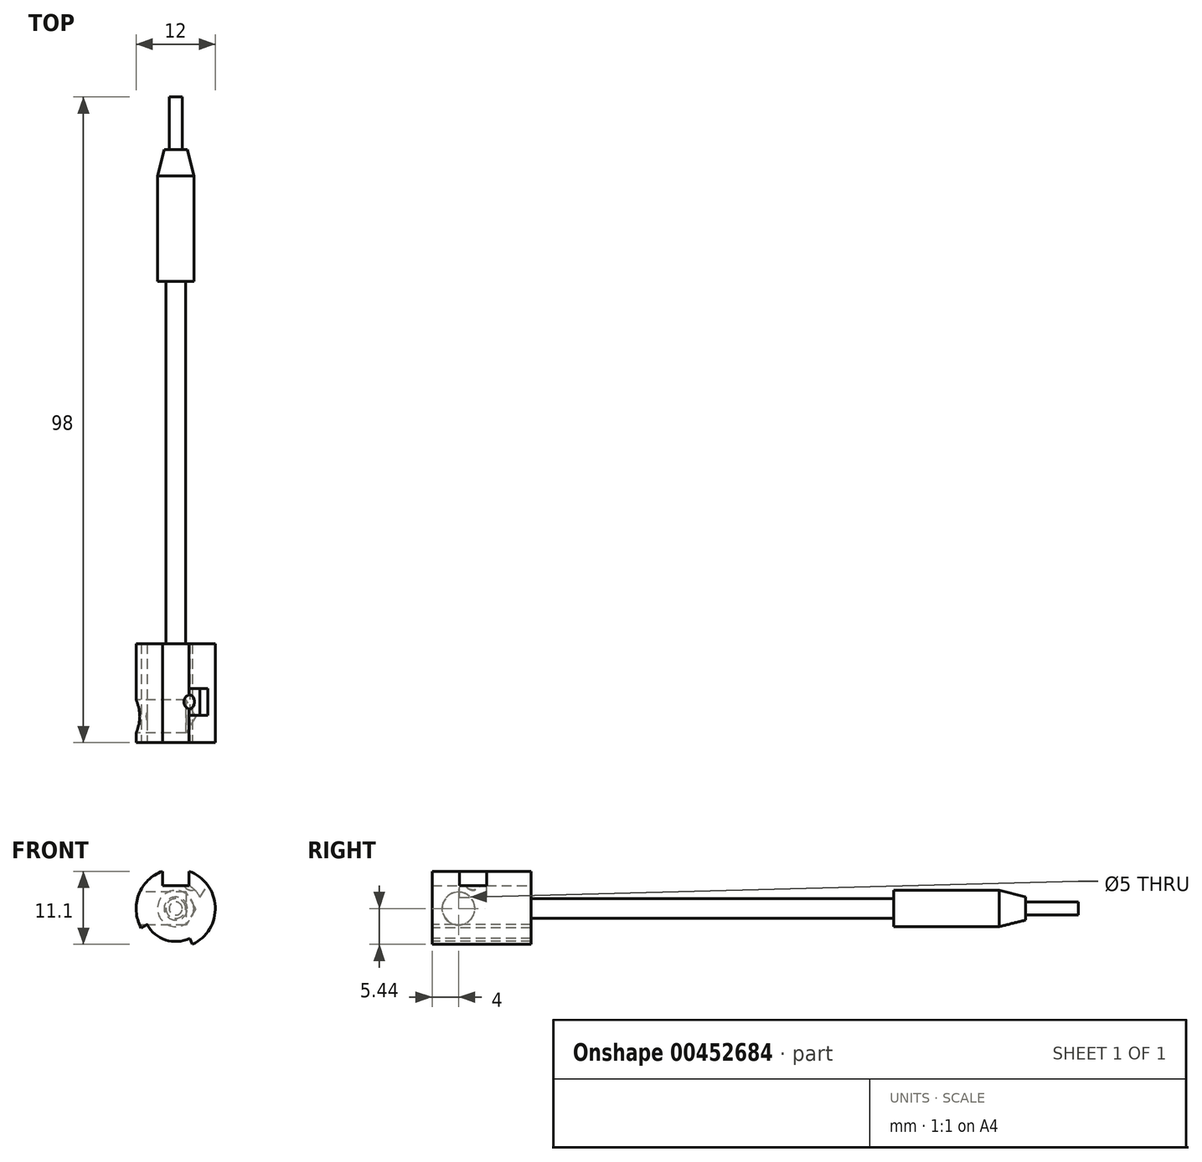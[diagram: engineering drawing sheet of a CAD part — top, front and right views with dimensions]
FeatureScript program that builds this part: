
annotation { "Feature Type Name" : "Feature", "Feature Type Description" : "" }
export const myFeature = defineFeature(function(context is Context, id is Id, definition is map)
    precondition{}
    {
        {
            var Q0;
            Q0=qCreatedBy(makeId("Front.planeOp"),FACE);
            var sketch = newSketch(context, id + "F0", { "sketchPlane" : qUnion([Q0])});
            skCircle(sketch, "E0", {"center": v(0, 0) * mm, "radius": 1 * mm});
            skSolve(sketch);
        }
        {
            var Q0;
            Q0=qSketchRegion(id+"F0",true);
            extrude(context, id + "F1", {"entities" : qUnion([Q0]), "oppositeDirection" : true, "depth" : 8 * mm});
        }
        {
            var Q0;
            Q0=makeQuery(id+"F1.opExtrude","CAP_FACE",FACE,{"disambiguationData":[OSD([sQuery(id+"F0.wireOp",EDGE,"E0")])],"isStart":true});
            var sketch = newSketch(context, id + "F2", { "sketchPlane" : qUnion([Q0])});
            skCircle(sketch, "E1", {"center": v(0, 0) * mm, "radius": 2.75 * mm});
            skSolve(sketch);
        }
        {
            var Q0;
            Q0=qSketchRegion(id+"F2",true);
            extrude(context, id + "F3", {"entities" : qUnion([Q0]), "operationType" : NewBodyOperationType.ADD, "depth" : 80 * mm});
        }
        {
            var Q0;
            Q0=makeQuery(id+"F3.opExtrude","CAP_EDGE",EDGE,{"disambiguationData":[OSD([sQuery(id+"F2.wireOp",EDGE,"E1")])],"isStart":true});
            chamfer(context, id + "F4", {"entities" : qUnion([Q0]), "chamferType" : ChamferType.TWO_OFFSETS, "width1" : 4 * mm, "oppositeDirection" : false, "width2" : 1 * mm, "tangentPropagation" : true});
        }
        {
            var Q0;
            Q0=makeQuery(id+"F3.opExtrude","CAP_FACE",FACE,{"disambiguationData":[OSD([sQuery(id+"F2.wireOp",EDGE,"E1")])],"isStart":false});
            var sketch = newSketch(context, id + "F5", { "sketchPlane" : qUnion([Q0])});
            skCircle(sketch, "E2", {"center": v(0, 0) * mm, "radius": 6 * mm});
            skSolve(sketch);
        }
        {
            var Q0;
            Q0=makeQuery(id+"F5.imprint","IMPRINT",FACE,{"disambiguationData":[TD([[makeQuery(id+"F5.imprint","IMPRINT",EDGE,{"derivedFrom":sQuery(id+"F5.wireOp",EDGE,"E2")}),1.0]])]});
            extrude(context, id + "F6", {"entities" : qUnion([Q0]), "operationType" : NewBodyOperationType.ADD, "oppositeDirection" : true, "depth" : 5 * mm});
        }
        {
            var Q0;
            Q0=makeQuery(id+"F6.boolean.opBoolean","MERGE",FACE,{"derivedFrom":[makeQuery(id+"F3.opExtrude","CAP_FACE",FACE,{"disambiguationData":[OSD([sQuery(id+"F2.wireOp",EDGE,"E1")])],"isStart":false}),makeQuery(id+"F6.opExtrude","CAP_FACE",FACE,{"disambiguationData":[OSD([sQuery(id+"F12.wireOp",EDGE,"E3"),sQuery(id+"F5.wireOp",EDGE,"E2")])],"isStart":true})]});
            extrude(context, id + "F7", {"entities" : qUnion([Q0]), "operationType" : NewBodyOperationType.ADD, "depth" : 10 * mm});
        }
        {
            var Q0;
            Q0=qCreatedBy(makeId("Right.planeOp"),FACE);
            cPlane(context, id + "F8", {"entities" : qUnion([Q0]), "cplaneType" : CPlaneType.OFFSET, "offset" : 6 * mm, "oppositeDirection" : true, "width" : 150 * mm, "height" : 150 * mm});
        }
        {
            var Q0;
            Q0=qCreatedBy(makeId("Top.planeOp"),FACE);
            cPlane(context, id + "F9", {"entities" : qUnion([Q0]), "cplaneType" : CPlaneType.OFFSET, "offset" : 6 * mm, "width" : 150 * mm, "height" : 150 * mm});
        }
        {
            var Q0;
            Q0=qCreatedBy(id+"F9.planeOp",FACE);
            var Q1;
            Q1=makeQuery(id+"F7.opExtrude","CAP_EDGE",EDGE,{"disambiguationData":[OSD([sQuery(id+"F5.wireOp",EDGE,"E2")])],"isStart":false});
            cPlane(context, id + "F10", {"entities" : qUnion([Q0, Q1]), "cplaneType" : CPlaneType.LINE_ANGLE, "offset" : 25 * mm, "angle" : 45 * degree, "width" : 150 * mm, "height" : 150 * mm});
        }
        {
            var Q0;
            Q0=qCreatedBy(id+"F10.planeOp",FACE);
            cPlane(context, id + "F11", {"entities" : qUnion([Q0]), "cplaneType" : CPlaneType.OFFSET, "offset" : 3.5 * mm, "width" : 150 * mm, "height" : 150 * mm});
        }
        {
            var Q0;
            Q0=makeQuery(id+"F6.opExtrude","CAP_FACE",FACE,{"disambiguationData":[OSD([sQuery(id+"F2.wireOp",EDGE,"E1"),sQuery(id+"F5.wireOp",EDGE,"E2")])],"isStart":false});
            var sketch = newSketch(context, id + "F12", { "sketchPlane" : qUnion([Q0])});
            skCircle(sketch, "E3", {"center": v(0, 0) * mm, "radius": 1.5 * mm});
            skCircle(sketch, "E4", {"center": v(0, 0) * mm, "radius": 2.75 * mm});
            skSolve(sketch);
        }
        {
            var Q0;
            Q0=makeQuery(id+"F12.imprint","IMPRINT",FACE,{"disambiguationData":[TD([[makeQuery(id+"F12.imprint","IMPRINT",EDGE,{"derivedFrom":sQuery(id+"F12.wireOp",EDGE,"E3")}),-1.0]])]});
            extrude(context, id + "F13", {"entities" : qUnion([Q0]), "operationType" : NewBodyOperationType.REMOVE, "depth" : 55 * mm});
        }
        {
            var Q0;
            Q0=qCreatedBy(id+"F8.planeOp",FACE);
            var sketch = newSketch(context, id + "F14", { "sketchPlane" : qUnion([Q0])});
            skPoint(sketch, "E5", {"position": v(-86, 0) * mm});
            skSolve(sketch);
        }
        {
            var Q0;
            Q0=sQuery(id+"F14.wireOp",VERTEX,"E5");
            var Q1;
            Q1=makeQuery(id+"F1.opExtrude","SWEPT_BODY",BODY,{"disambiguationData":[OSD([sQuery(id+"F0.wireOp",EDGE,"E0")])]});
            hole(context, id + "F15", {"style" : HoleStyle.SIMPLE, "endStyle" : HoleEndStyle.BLIND, "oppositeDirection" : true, "standardTappedOrClearance" : lookupTablePath({ "standard" : "ISO", "engagement" : "75%", "pitch" : "1 mm", "size" : "M6", "type" : "Tapped" }), "standardBlindInLast" : lookupTablePath({ "standard" : "ISO", "engagement" : "75%", "pitch" : "1 mm", "size" : "M6", "type" : "Tapped" }), "holeDiameter" : 5 * mm, "showTappedDepth" : true, "holeDepth" : 7 * mm, "isTappedThrough" : true, "tappedDepth" : 4 * mm, "tapClearance" : 3, "locations" : qUnion([Q0]), "scope" : qUnion([Q1]), "majorDiameter" : 6 * mm});
        }
        {
            var Q0;
            Q0=qCreatedBy(id+"F9.planeOp",FACE);
            var sketch = newSketch(context, id + "F16", { "sketchPlane" : qUnion([Q0])});
            skLineSegment(sketch, "E6.bottom", {"start": v(-2, -90) * mm, "end": v(2, -90) * mm});
            skLineSegment(sketch, "E6.top", {"start": v(-2, -75) * mm, "end": v(2, -75) * mm});
            skLineSegment(sketch, "E6.left", {"start": v(-2, -90) * mm, "end": v(-2, -75) * mm});
            skLineSegment(sketch, "E6.right", {"start": v(2, -90) * mm, "end": v(2, -75) * mm});
            skLineSegment(sketch, "E7", {"start": v(0, -90) * mm, "end": v(0, -75) * mm, "construction": true});
            skSolve(sketch);
        }
        {
            var Q0;
            Q0=qSketchRegion(id+"F16",true);
            extrude(context, id + "F17", {"entities" : qUnion([Q0]), "operationType" : NewBodyOperationType.REMOVE, "oppositeDirection" : true, "depth" : 2.5 * mm});
        }
        {
            var Q0;
            Q0=makeQuery(id+"F7.opExtrude","CAP_FACE",FACE,{"disambiguationData":[OSD([sQuery(id+"F2.wireOp",EDGE,"E1"),sQuery(id+"F5.wireOp",EDGE,"E2")])],"isStart":false});
            cPlane(context, id + "F18", {"entities" : qUnion([Q0]), "cplaneType" : CPlaneType.OFFSET, "offset" : 6.2 * mm, "oppositeDirection" : true, "width" : 150 * mm, "height" : 150 * mm});
        }
        {
            var Q0;
            Q0=makeQuery(id+"F17.boolean.opBoolean","COPY",FACE,{"derivedFrom":makeQuery(id+"F17.opExtrude","SWEPT_FACE",FACE,{"disambiguationData":[OSD([sQuery(id+"F16.wireOp",EDGE,"E6.right")])]})});
            var sketch = newSketch(context, id + "F19", { "sketchPlane" : qUnion([Q0])});
            skLineSegment(sketch, "E8.bottom", {"start": v(81.75, 5.66) * mm, "end": v(85.85, 5.66) * mm});
            skLineSegment(sketch, "E8.top", {"start": v(81.75, 3.5) * mm, "end": v(85.85, 3.5) * mm});
            skLineSegment(sketch, "E8.left", {"start": v(85.85, 3.5) * mm, "end": v(85.85, 5.66) * mm});
            skLineSegment(sketch, "E8.right", {"start": v(81.75, 3.5) * mm, "end": v(81.75, 5.66) * mm});
            skLineSegment(sketch, "E9", {"start": v(83.8, 5.66) * mm, "end": v(83.8, 3.5) * mm, "construction": true});
            skSolve(sketch);
        }
        {
            var Q0;
            Q0=qSketchRegion(id+"F19",true);
            var Q1;
            {var subQ0=sQuery(id+"F5.wireOp",EDGE,"E2");Q1=makeQuery(id+"F17.boolean.opBoolean","SPLIT",FACE,{"disambiguationData":[TD([makeQuery(id+"FctZoTc2OwpmKR8_1.boolean.opBoolean","COPY",FACE,{"derivedFrom":makeQuery(id+"FctZoTc2OwpmKR8_1.opExtrude","SWEPT_FACE",FACE,{"disambiguationData":[OSD([sQuery(id+"Fsz8UjHsgXwGy4J_1.wireOp",EDGE,"ASJJtbLU-RnPE-262p-RrrI-WQdVs2qlrqvg.left")])]})})])],"derivedFrom":makeQuery(id+"F7.boolean.opBoolean","MERGE",FACE,{"derivedFrom":[makeQuery(id+"F6.opExtrude","SWEPT_FACE",FACE,{"disambiguationData":[OSD([subQ0])]}),makeQuery(id+"F7.opExtrude","SWEPT_FACE",FACE,{"disambiguationData":[OSD([subQ0])]})]})});}
            revolve(context, id + "F20", {"operationType" : NewBodyOperationType.REMOVE, "entities" : qUnion([Q0]), "axis" : qUnion([Q1]), "revolveType" : RevolveType.ONE_DIRECTION, "oppositeDirection" : true, "angle" : 35 * degree});
        }
        {
            var Q0;
            Q0=qCreatedBy(makeId("Top.planeOp"),FACE);
            var Q1;
            {var subQ0=sQuery(id+"F5.wireOp",EDGE,"E2");Q1=makeQuery(id+"F17.boolean.opBoolean","SPLIT",EDGE,{"disambiguationData":[TD([makeQuery(id+"FctZoTc2OwpmKR8_1.boolean.opBoolean","COPY",FACE,{"derivedFrom":makeQuery(id+"FctZoTc2OwpmKR8_1.opExtrude","SWEPT_FACE",FACE,{"disambiguationData":[OSD([sQuery(id+"Fsz8UjHsgXwGy4J_1.wireOp",EDGE,"ASJJtbLU-RnPE-262p-RrrI-WQdVs2qlrqvg.left")])]})})])],"derivedFrom":makeQuery(id+"F7.opExtrude","CAP_EDGE",EDGE,{"disambiguationData":[OSD([subQ0])],"isStart":false})});}
            cPlane(context, id + "F21", {"entities" : qUnion([Q0, Q1]), "cplaneType" : CPlaneType.LINE_ANGLE, "offset" : 25 * mm, "angle" : 35 * degree, "oppositeDirection" : true, "width" : 150 * mm, "height" : 150 * mm});
        }
        {
            var Q0;
            Q0=qCreatedBy(id+"F21.planeOp",FACE);
            var Q1;
            Q1=makeQuery(id+"F20.boolean.opBoolean","MERGE",EDGE,{"derivedFrom":[makeQuery(id+"F17.boolean.opBoolean","COPY",EDGE,{"derivedFrom":makeQuery(id+"F17.opExtrude","CAP_EDGE",EDGE,{"disambiguationData":[OSD([sQuery(id+"F16.wireOp",EDGE,"E6.right")])],"isStart":false})}),makeQuery(id+"F20.opRevolve","CAP_EDGE",EDGE,{"disambiguationData":[OSD([sQuery(id+"F19.wireOp",EDGE,"E8.top")]),OD(0.0)],"isStart":false})]});
            cPlane(context, id + "F22", {"entities" : qUnion([Q0, Q1]), "cplaneType" : CPlaneType.LINE_ANGLE, "offset" : 25 * mm, "angle" : 0 * degree, "width" : 150 * mm, "height" : 150 * mm});
        }
        {
            var Q0;
            Q0=qCreatedBy(id+"F22.planeOp",FACE);
            var Q1;
            Q1=makeQuery(id+"F20.boolean.opBoolean","MERGE",EDGE,{"derivedFrom":[makeQuery(id+"F17.boolean.opBoolean","COPY",EDGE,{"derivedFrom":makeQuery(id+"F17.opExtrude","CAP_EDGE",EDGE,{"disambiguationData":[OSD([sQuery(id+"F16.wireOp",EDGE,"E6.right")])],"isStart":false})}),makeQuery(id+"F20.opRevolve","CAP_EDGE",EDGE,{"disambiguationData":[OSD([sQuery(id+"F19.wireOp",EDGE,"E8.top")]),OD(0.0)],"isStart":false})]});
            cPlane(context, id + "F23", {"entities" : qUnion([Q0, Q1]), "cplaneType" : CPlaneType.LINE_ANGLE, "offset" : 25 * mm, "angle" : 90 * degree, "width" : 150 * mm, "height" : 150 * mm});
        }
        {
            var Q0;
            Q0=qCreatedBy(id+"F22.planeOp",FACE);
            var sketch = newSketch(context, id + "F24", { "sketchPlane" : qUnion([Q0])});
            skPoint(sketch, "E10", {"position": v(-0.37, -83.8) * mm});
            skCircle(sketch, "E11", {"center": v(-0.37, -83.8) * mm, "radius": 1.25 * mm, "construction": true});
            skSolve(sketch);
        }
        {
            var Q0;
            Q0=qCreatedBy(id+"F23.planeOp",FACE);
            var sketch = newSketch(context, id + "F25", { "sketchPlane" : qUnion([Q0])});
            skLineSegment(sketch, "E12", {"start": v(83.8, 3.41) * mm, "end": v(83.8, 5.91) * mm});
            skArc(sketch, "E13", {"start": v(83.8, 3.41) * mm, "mid": v(85.05, 4.66) * mm, "end": v(83.8, 5.91) * mm});
            skSolve(sketch);
        }
        {
            var Q0;
            Q0 = qSketchRegion(id + "F25", true);
            var Q1;
            Q1=sQuery(id+"F25.wireOp",EDGE,"E13");
            var Q2;
            Q2=sQuery(id+"F25.wireOp",EDGE,"E12");
            revolve(context, id + "F26", {"operationType" : NewBodyOperationType.REMOVE, "entities" : qUnion([Q0]), "surfaceEntities" : qUnion([Q1]), "axis" : qUnion([Q2]), "revolveType" : RevolveType.FULL});
        }
        {
            var Q0;
            Q0=makeQuery(id+"F7.opExtrude","CAP_FACE",FACE,{"disambiguationData":[OSD([sQuery(id+"F2.wireOp",EDGE,"E1"),sQuery(id+"F5.wireOp",EDGE,"E2")])],"isStart":false});
            var sketch = newSketch(context, id + "F27", { "sketchPlane" : qUnion([Q0])});
            skCircle(sketch, "E14", {"center": v(0, 0) * mm, "radius": 6 * mm});
            skCircle(sketch, "E15", {"center": v(0, 0) * mm, "radius": 5 * mm});
            skLineSegment(sketch, "E16", {"start": v(0, 0) * mm, "end": v(2.54, -5.44) * mm});
            skLineSegment(sketch, "E17", {"start": v(0, 0) * mm, "end": v(-5.25, -2.9) * mm});
            skLineSegment(sketch, "E18", {"start": v(0, 0) * mm, "end": v(0, -6) * mm, "construction": true});
            skSolve(sketch);
        }
        {
            var Q0;
            {var subQ0=sQuery(id+"F27.wireOp",EDGE,"E16");var subQ1=sQuery(id+"F27.wireOp",EDGE,"E14");var subQ2=makeQuery(id+"F27.imprint","INTERSECT",VERTEX,{"derivedFrom":[subQ1,subQ0]});Q0=makeQuery(id+"F27.imprint","IMPRINT",FACE,{"disambiguationData":[TD([[makeQuery(id+"F27.imprint","IMPRINT",EDGE,{"disambiguationData":[TD([[subQ2,1.0]])],"derivedFrom":subQ1}),1.0]])]});}
            extrude(context, id + "F28", {"entities" : qUnion([Q0]), "operationType" : NewBodyOperationType.REMOVE, "oppositeDirection" : true, "depth" : 15 * mm});
        }
    });
